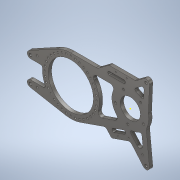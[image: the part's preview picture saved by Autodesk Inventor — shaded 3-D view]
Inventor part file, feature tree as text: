
AUTODESK INVENTOR PART (.ipt)
format: ipt  version: 2021 (Build 250183000, 183)  size: 573,952 bytes
history: native  units: in
note: dims shown in document units (in); Inventor stores cm internally (conversion verified against a paired STEP export)
features: sketch x22, extrude x16, hole x5, fillet x2, chamfer x1, projected_geometry x1
ambient origin geometry x8: Origin, YZ Plane, XZ Plane, XY Plane, X Axis, Y Axis, Z Axis, Center Point
bodies: Body1 (feature_tree)
feature tree (47):
  extrude  "Extrusion13"  Depth=0.5in TaperAngle=0.0deg
  hole  "Hole4"  [1 undecoded]
  extrude  "Extrusion14"  Depth=0.5in TaperAngle=0.0deg
  extrude  "Extrusion15"  Depth=5.0in
  extrude  "Extrusion16"  Depth=1.0in
  hole  "Hole6"  [1 undecoded]
  extrude  "Extrusion17"  Depth=0.5in TaperAngle=0.0deg
  hole  "Hole7"  [1 undecoded]
  hole  "Hole9"  [1 undecoded]
  hole  "Hole10"  [1 undecoded]
  extrude  "Extrusion18"  Depth=1.0in
  extrude  "Extrusion19"  Depth=1.0in
  sketch  "Sketch33"  dims[d183=0.257in d184=0.75in d185=0.438in d186=0.25in d187=0.5635in d188=1.0in d189=0.8108in d191=1.0in]
  extrude  "Extrusion21"  Depth=0.239in
  extrude  "Extrusion22"  Depth=0.5in
  extrude  "Extrusion23"  Depth=1.0in
  extrude  "Extrusion24"  Depth=0.75in
  fillet  "Fillet2"  Radius=0.75in
  extrude  "Extrusion25"  Depth=0.25in
  extrude  "Extrusion26"  Depth=1.0in TaperAngle=0.0deg
  fillet  "Fillet3"  Radius=0.25in
  extrude  "Extrusion27"  Depth=0.75in
  chamfer  "Chamfer1"  Distance=0.75in
  sketch  "Sketch40"  dims[d214=0.5in d215=1.0in d216=0.0in d217=0.25in]
  extrude  "Extrusion28"  Depth=0.25in
  extrude  "Extrusion29"  Depth=1.0in TaperAngle=0.0deg
  sketch  "Sketch14"  dims[d96=8.5in d97=2.16in d98=9.0in d99=5.5in d100=1.0in d101=1.0in d102=6.0in d103=6.0in d104=3.718in d105=1.0in d108=10.718in d109=1.5in d111=0.5in d112=0.0in]
  sketch  "Sketch15"  dims[d113=0.386in d114=0.75in d115=0.762in d116=0.25in d117=0.5635in d118=0.484in d119=0.8108in d120=3.5in]
  sketch  "Sketch16"  dims[d121=6.75in d122=0.5in d123=0.0in]
  sketch  "Sketch18"  dims[d132=5.0in d133=17.223in]
  sketch  "Sketch19"  dims[d134=1.0in d135=1.0in]
  sketch  "Sketch20"  dims[d136=0.5in d137=0.0in d138=1.0in]
  sketch  "Sketch21"  dims[d140=4.0in d141=0.5in d142=0.0in]
  sketch  "Sketch23"  dims[d143=1.0in d144=1.625in]
  sketch  "Sketch27"  dims[d145=0.177in d146=0.75in d147=0.332in d148=0.25in d149=0.5635in d150=0.484in d151=0.8108in d155=1.0in d156=0.0in]
  sketch  "Sketch29"  dims[d157=1.625in]
  sketch  "Sketch31"  dims[d159=0.177in d160=0.75in d161=0.332in d162=0.25in d163=0.5635in d164=1.0in d165=0.8108in d178=7.75in]
  sketch  "Sketch32"  dims[d179=3.5433in d181=360.0deg]
  sketch  "Sketch34"  dims[d192=0.0481in d193=1.0in]
  sketch  "Sketch35"  dims[d194=0.3526in d197=0.239in]
  sketch  "Sketch36"  dims[d198=0.1195in d199=0.5in]
  sketch  "Sketch37"  dims[d200=0.266in d201=0.75in d202=0.507in d203=0.25in d204=0.5635in d205=1.0in d206=0.8108in d207=0.1718in]
  sketch  "Sketch38"  dims[d208=15.0deg d210=0.75in d211=0.75in]
  sketch  "Sketch39"  dims[d212=0.75in d213=0.25in]
  sketch  "Sketch41"  dims[d218=1.0in d219=0.0in d220=0.75in]
  sketch  "Sketch42"  dims[d221=0.5in d223=0.75in d231=0.25in d232=1.0in d233=0.0in d234=0.25in d235=1.0in d236=0.0in d237=0.75in d238=1.0in d239=0.0in d240=0.5in d241=0.5in d242=1.0in d243=0.0in d244=0.25in d247=0.75in d249=0.75in d250=0.5in d251=2.8in d252=0.375in d253=1.25in d255=0.75in d256=0.75in d257=1.0in d258=0.0in d259=0.25in d260=1.0in d261=0.0in d262=0.25in d263=0.5in d264=1.0in d265=0.0in d266=0.0156in d267=0.125in d268=45.0deg d270=1.9685in d271=0.452in d272=0.48in d273=360.0deg d274=45.0deg d275=0.325in d276=1.0in d277=0.0in d278=1.9685in d280=360.0deg d282=3.005in d283=3.005in d284=1.0in d285=0.0in d286=0.0344in]
  projected_geometry  "Project Cut Edges1"
note: 5 required parameter values undecoded (feature->parameter linkage not recoverable at this tier; creation-order binding heuristic only, values carry confidence <= 0.55)
